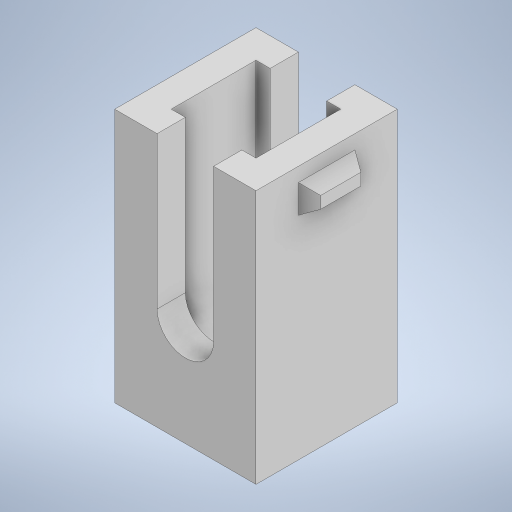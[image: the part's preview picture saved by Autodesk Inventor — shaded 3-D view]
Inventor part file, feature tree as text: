
AUTODESK INVENTOR PART (.ipt)
format: ipt  version: 2023 (Build 270158000, 158)  size: 253,952 bytes
history: native  units: in
note: dims shown in document units (in); Inventor stores cm internally (conversion verified against a paired STEP export)
features: extrude x5, sketch x5, shell x1
ambient origin geometry x8: Origin, YZ Plane, XZ Plane, XY Plane, X Axis, Y Axis, Z Axis, Center Point
bodies: Solid1 (feature_tree)
feature tree (11):
  extrude  "Extrusion1"  Depth=0.1969in
  shell  "Shell1"  Thickness=0.3543in
  extrude  "Extrusion4"  Depth=0.0394in
  extrude  "Extrusion5"  Depth=0.0394in
  extrude  "Extrusion6"  Depth=0.0394in
  extrude  "Extrusion7"  Depth=0.0394in
  sketch  "Sketch1"  dims[d0=0.1969in d1=0.1969in d2=0.3543in d3=0.0in]
  sketch  "Sketch9"  dims[d4=0.0394in d10=0.0394in]
  sketch  "Sketch10"  dims[d11=0.0197in d12=-0.2061in d13=0.0394in]
  sketch  "Sketch11"  dims[d14=0.0787in d15=0.0394in]
  sketch  "Sketch12"  dims[d16=0.0787in d17=0.0394in d18=0.0197in d19=-0.2061in d20=0.0787in d21=0.0in d22=0.0in d23=0.0787in d24=0.0in d25=0.0in d26=0.0197in d27=0.0344in d28=0.0197in d29=0.0344in]
